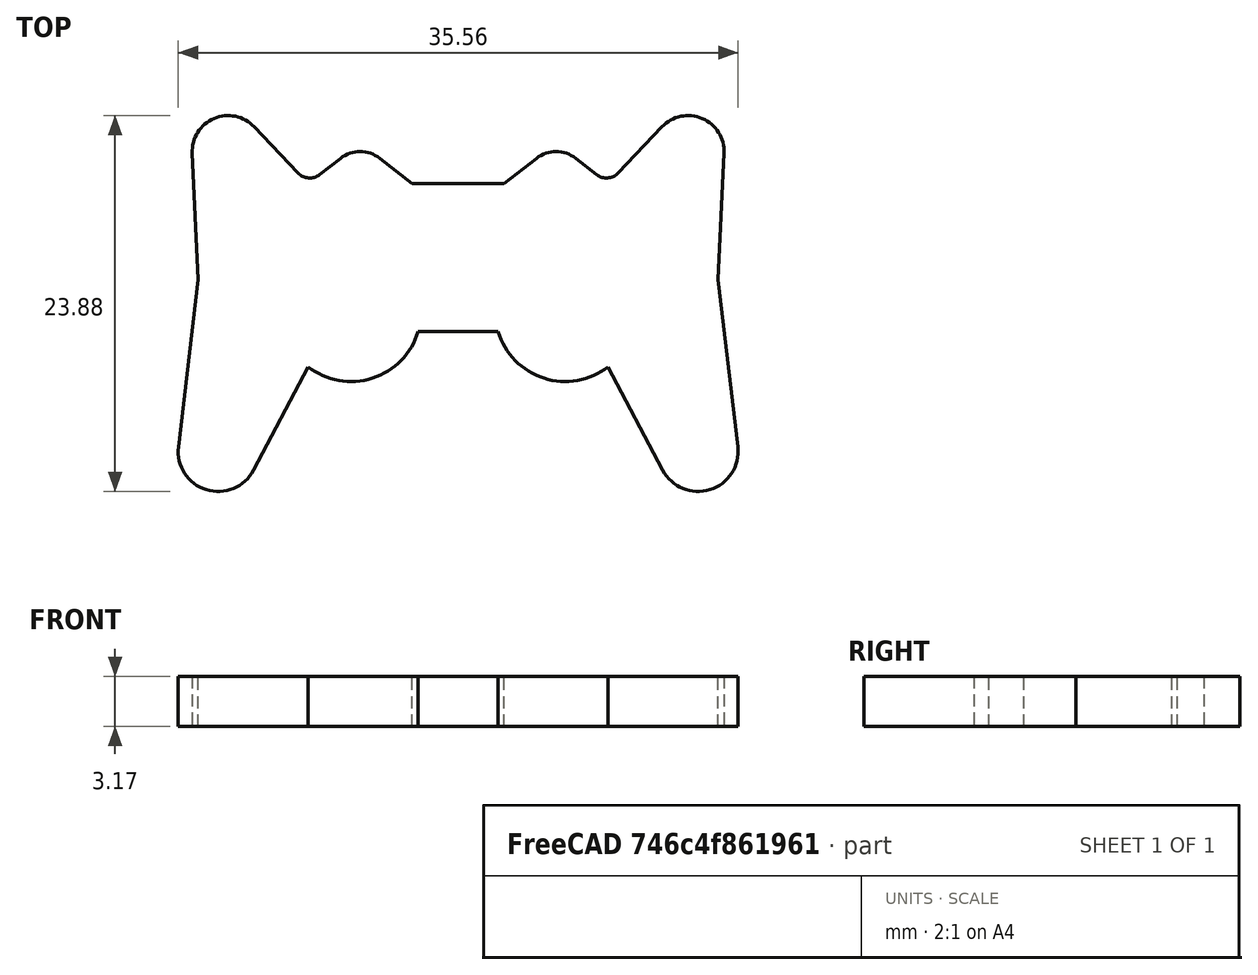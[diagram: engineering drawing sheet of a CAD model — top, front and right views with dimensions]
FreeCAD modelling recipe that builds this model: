
FCSTD DOCUMENT  (FreeCAD 0.20R26720 (Git))
Label: Operator_Template
License: All rights reserved
LicenseURL: http://en.wikipedia.org/wiki/All_rights_reserved
objects: TechDraw::DrawViewDimExtent×2, Sketcher::SketchObject×1, PartDesign::Pad×1, TechDraw::DrawSVGTemplate×1, PartDesign::Fillet×1, PartDesign::Body×1, TechDraw::DrawProjGroupItem×1, TechDraw::DrawProjGroup×1, TechDraw::DrawPage×1
note: 6 computed .brp shape members not serialized (recipe doc carries the construction recipe); baked Part::Feature solids carry a one-line shape summary decoded from their .brp

FEATURE [Sketcher::SketchObject] Sketch
  FullyConstrained = true
  MapMode = 5
  Support = -> [XY_Plane]
  sketch-geometry (32):
    g0: LineSegment StartX=-16.51 StartY=3.302 StartZ=0 EndX=-17.7625 EndY=-7.32262 EndZ=0
    g1: LineSegment StartX=-12.9943 StartY=-8.80672 StartZ=0 EndX=-9.525 EndY=-2.24153 EndZ=0
    g2: LineSegment StartX=-2.54 StartY=0 StartZ=0 EndX=2.54 EndY=0 EndZ=0
    g3: LineSegment StartX=9.525 StartY=-2.24153 StartZ=0 EndX=12.9943 EndY=-8.80672 EndZ=0
    g4: LineSegment StartX=17.7625 StartY=-7.32262 StartZ=0 EndX=16.51 EndY=3.302 EndZ=0
    g5: LineSegment StartX=16.51 StartY=3.302 StartZ=0 EndX=16.8885 EndY=11.3222 EndZ=0
    g6: LineSegment StartX=12.9468 StartY=13.0036 StartZ=0 EndX=9.525 EndY=9.398 EndZ=0
    g7: LineSegment StartX=9.525 StartY=9.398 StartZ=0 EndX=7.47346 EndY=10.9997 EndZ=0
    g8: LineSegment StartX=4.97254 StartY=10.9997 StartZ=0 EndX=2.921 EndY=9.398 EndZ=0
    g9: LineSegment StartX=2.921 StartY=9.398 StartZ=0 EndX=-2.921 EndY=9.398 EndZ=0
    g10: LineSegment StartX=-2.921 StartY=9.398 StartZ=0 EndX=-4.97254 EndY=10.9997 EndZ=0
    g11: LineSegment StartX=-7.47346 StartY=10.9997 StartZ=0 EndX=-9.525 EndY=9.398 EndZ=0
    g12: LineSegment StartX=-9.525 StartY=9.398 StartZ=0 EndX=-12.9468 EndY=13.0036 EndZ=0
    g13: LineSegment StartX=-16.8885 StartY=11.3222 StartZ=0 EndX=-16.51 EndY=3.302 EndZ=0
    g14: ArcOfCircle CenterX=-6.79971 CenterY=1.27 CenterZ=0 NormalX=0 NormalY=0 NormalZ=1 AngleXU=0 Radius=4.445 StartAngle=4.05239 EndAngle=5.99343
    g15: ArcOfCircle CenterX=6.79971 CenterY=1.27 CenterZ=0 NormalX=0 NormalY=0 NormalZ=1 AngleXU=0 Radius=4.445 StartAngle=3.43134 EndAngle=5.37239
    g16: ArcOfCircle CenterX=-14.605 CenterY=11.43 CenterZ=0 NormalX=0 NormalY=0 NormalZ=1 AngleXU=0 Radius=2.286 StartAngle=0.759251 EndAngle=3.18875
    g17: ArcOfCircle CenterX=14.605 CenterY=11.43 CenterZ=0 NormalX=0 NormalY=0 NormalZ=1 AngleXU=0 Radius=2.286 StartAngle=6.23603 EndAngle=8.66553
    g18: ArcOfCircle CenterX=15.24 CenterY=-7.62 CenterZ=0 NormalX=0 NormalY=0 NormalZ=1 AngleXU=0 Radius=2.54 StartAngle=3.62773 EndAngle=6.40053
    g19: ArcOfCircle CenterX=-15.24 CenterY=-7.62 CenterZ=0 NormalX=0 NormalY=0 NormalZ=1 AngleXU=0 Radius=2.54 StartAngle=3.02424 EndAngle=5.79705
    g20: LineSegment StartX=-6.79971 StartY=1.27 StartZ=0 EndX=6.79971 EndY=1.27 EndZ=0
    g21: LineSegment StartX=-15.24 StartY=-7.62 StartZ=0 EndX=15.24 EndY=-7.62 EndZ=0
    g22: LineSegment StartX=0 StartY=0 StartZ=0 EndX=0 EndY=-7.62 EndZ=0
    g23: LineSegment StartX=-16.51 StartY=3.302 StartZ=0 EndX=16.51 EndY=3.302 EndZ=0
    g24: LineSegment StartX=0 StartY=0 StartZ=0 EndX=0 EndY=3.302 EndZ=0
    g25: LineSegment StartX=-14.605 StartY=11.43 StartZ=0 EndX=14.605 EndY=11.43 EndZ=0
    g26: LineSegment StartX=0 StartY=3.302 StartZ=0 EndX=0 EndY=11.43 EndZ=0
    g27: ArcOfCircle CenterX=-6.223 CenterY=9.398 CenterZ=0 NormalX=0 NormalY=0 NormalZ=1 AngleXU=0 Radius=2.032 StartAngle=0.907923 EndAngle=2.23367
    g28: ArcOfCircle CenterX=6.223 CenterY=9.398 CenterZ=0 NormalX=0 NormalY=0 NormalZ=1 AngleXU=0 Radius=2.032 StartAngle=0.907923 EndAngle=2.23367
    g29: LineSegment StartX=-9.525 StartY=9.398 StartZ=0 EndX=9.525 EndY=9.398 EndZ=0
    g30: LineSegment StartX=-6.223 StartY=9.398 StartZ=0 EndX=6.223 EndY=9.398 EndZ=0
    g31: LineSegment StartX=-9.525 StartY=-2.24153 StartZ=0 EndX=9.525 EndY=-2.24153 EndZ=0
  constraints (79):
    c: Coincident(g4,g5)
    c: Coincident(g6,g7)
    c: Coincident(g8,g9)
    c: Horizontal(g9)
    c: Coincident(g9,g10)
    c: Coincident(g11,g12)
    c: Coincident(g13,g0)
    c: Coincident(g14,g2)
    c: Coincident(g15,g2)
    c: Equal(g14,g15)
    c: Symmetric(g2,g2,g-1)
    c: Tangent(g13,g16) = -1.5708
    c: Tangent(g12,g16) = -1.5708
    c: Tangent(g6,g17) = -1.5708
    c: Tangent(g5,g17) = -1.5708
    c: Tangent(g3,g18) = -1.5708
    c: Tangent(g4,g18) = -1.5708
    c: Tangent(g0,g19) = -1.5708
    c: Tangent(g1,g19) = -1.5708
    c: Distance(g2) = 5.08
    c: Diameter(g14) = 8.89
    c: Coincident(g20,g14)
    c: Coincident(g20,g15)
    c: Horizontal(g20)
    c: Distance(g2,g20) = 1.27
    c: Equal(g19,g18)
    c: Coincident(g21,g19)
    c: Coincident(g21,g18)
    c: Horizontal(g21)
    c: Coincident(g22,g-1)
    c: Vertical(g22)
    c: Symmetric(g19,g18,g22)
    c: DistanceX(g0,g4) = 33.02
    c: Distance(g21) = 30.48
    c: Diameter(g19) = 5.08
    c: Distance(g22) = 7.62
    c: Coincident(g23,g0)
    c: Coincident(g23,g4)
    c: Horizontal(g23)
    c: Coincident(g24,g-1)
    c: Vertical(g24)
    c: Symmetric(g0,g4,g24)
    c: Distance(g24) = 3.302
    c: Equal(g17,g16)
    c: Coincident(g25,g16)
    c: Coincident(g25,g17)
    c: Horizontal(g25)
    c: Coincident(g26,g24)
    c: Symmetric(g16,g17,g26)
    c: Distance(g26) = 8.128
    c: Diameter(g16) = 4.572
    c: Distance(g25) = 29.21
    c: Tangent(g11,g27) = -1.5708
    c: Tangent(g10,g27) = -1.5708
    c: Tangent(g8,g28) = -1.5708
    c: Tangent(g7,g28) = -1.5708
    c: Symmetric(g9,g8,g26)
    c: Coincident(g29,g11)
    c: Coincident(g29,g6)
    c: Tangent(g29,g9)
    c: Equal(g7,g8)
    c: Equal(g10,g11)
    c: Equal(g10,g8)
    c: Coincident(g30,g27)
    c: Coincident(g30,g28)
    c: Horizontal(g30)
    c: Equal(g28,g27)
    c: PointOnObject(g27,g29)
    c: Diameter(g27) = 4.064
    c: Distance(g8,g20) = 8.128
    c: Distance(g11,g6) = 19.05
    c: Distance(g9) = 5.842
    c: Horizontal(g2)
    c: Coincident(g15,g3)
    c: Coincident(g14,g1)
    c: Coincident(g31,g1)
    c: Coincident(g31,g3)
    c: Horizontal(g31)
    c: Distance(g31) = 19.05
FEATURE [PartDesign::Pad] Pad
  Direction = (0,0,1)
  Length = 3.175
  Length2 = 100.076
  Profile = -> Sketch
  ReferenceAxis = -> Sketch [N_Axis]
  Type = 0
FEATURE [TechDraw::DrawSVGTemplate] Template
  EditableTexts = Designed_by_Name=Design by Matthew; Drawing_number=01824f14; FC-Date=Dec 2021; FC-SC=1:1; FC-SH=1 of 1; FC-Title=Operator Patch; Subtitle=Tidal Force Robotics; Weight=0.01
  Height = 210
  Orientation = 1
  Width = 297
FEATURE [PartDesign::Fillet] Fillet
  Base = -> Pad [Edge56,Edge35]
  BaseFeature = -> Pad
  Radius = 1.016
  SupportTransform = false
FEATURE [PartDesign::Body] Body  label="Operator Template Body"
  Group = -> [Sketch,Pad,Fillet]
  Origin = -> Origin
  Tip = -> Fillet
FEATURE [TechDraw::DrawProjGroupItem] ProjItem  label="Front"
  CoarseView = false
  Direction = (0,0,1)
  Focus = 100
  HardHidden = false
  IsoCount = 0
  IsoHidden = false
  IsoVisible = false
  LockPosition = true
  Perspective = false
  Rotation = 0
  RotationVector = (1,0,0)
  ScaleType = 2
  SeamHidden = false
  SeamVisible = true
  SmoothHidden = false
  SmoothVisible = true
  Source = -> [Body]
  Type = 0
  X = 0
  XDirection = (1,0,0)
  Y = 0
FEATURE [TechDraw::DrawProjGroup] ProjGroup
  Anchor = -> ProjItem
  AutoDistribute = true
  LockPosition = false
  ProjectionType = 0
  Rotation = 0
  ScaleType = 0
  Source = -> [Body]
  Views = -> [ProjItem]
  X = 148.5
  Y = 105
  spacingX = 14.986
  spacingY = 14.986
FEATURE [TechDraw::DrawViewDimExtent] DimExtent
  Arbitrary = false
  ArbitraryTolerances = false
  CosmeticTags = 4876a07e-5734-4a42-9c70-3ad1e6a7d9bc | d5695a1d-5df9-4573-af45-24d7c8faea45
  DirExtent = 0
  EqualTolerance = true
  FormatSpec = %.3f
  FormatSpecOverTolerance = %+.3f
  FormatSpecUnderTolerance = %+.3f
  Inverted = false
  LockPosition = false
  MeasureType = 1
  OverTolerance = 0
  References2D = -> [ProjItem]
  Rotation = 0
  ScaleType = 0
  Source = -> [ProjItem]
  TheoreticalExact = false
  Type = 1
  UnderTolerance = 0
  X = 0.802663
  Y = -28.3225
FEATURE [TechDraw::DrawViewDimExtent] DimExtent001
  Arbitrary = false
  ArbitraryTolerances = false
  CosmeticTags = cb7f4163-6724-4b0a-a852-f6ca696e9f43 | 79479888-a2d5-4abe-9f57-d4747772a0c1
  DirExtent = 1
  EqualTolerance = true
  FormatSpec = %.3f
  FormatSpecOverTolerance = %+.3f
  FormatSpecUnderTolerance = %+.3f
  Inverted = false
  LockPosition = false
  MeasureType = 1
  OverTolerance = 0
  References2D = -> [ProjItem]
  Rotation = 0
  ScaleType = 0
  Source = -> [ProjItem]
  TheoreticalExact = false
  Type = 2
  UnderTolerance = 0
  X = 31.3039
  Y = 1.83466
FEATURE [TechDraw::DrawPage] Page
  KeepUpdated = true
  NextBalloonIndex = 1
  ProjectionType = 0
  Template = -> Template
  Views = -> [ProjGroup,DimExtent,DimExtent001]
